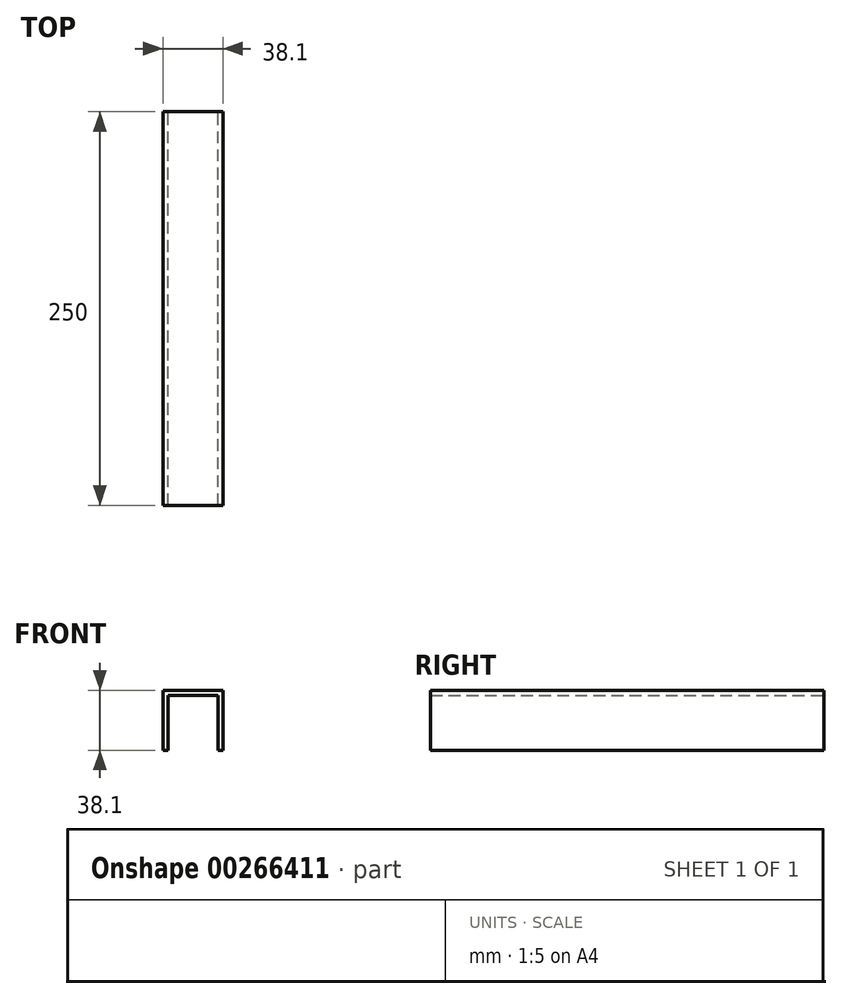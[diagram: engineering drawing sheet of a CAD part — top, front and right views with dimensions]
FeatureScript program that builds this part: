
annotation { "Feature Type Name" : "Feature", "Feature Type Description" : "" }
export const myFeature = defineFeature(function(context is Context, id is Id, definition is map)
    precondition{}
    {
        {
            var Q0;
            Q0=qCreatedBy(makeId("Front.planeOp"),FACE);
            var sketch = newSketch(context, id + "F0", { "sketchPlane" : qUnion([Q0])});
            skLineSegment(sketch, "E0.bottom", {"start": v(19.05, -19.05) * mm, "end": v(-19.05, -19.05) * mm});
            skLineSegment(sketch, "E0.top", {"start": v(19.05, 19.05) * mm, "end": v(-19.05, 19.05) * mm});
            skLineSegment(sketch, "E0.left", {"start": v(19.05, -19.05) * mm, "end": v(19.05, 19.05) * mm});
            skLineSegment(sketch, "E0.right", {"start": v(-19.05, -19.05) * mm, "end": v(-19.05, 19.05) * mm});
            skPoint(sketch, "E0.middle", {"position": v(0, 0) * mm});
            skLineSegment(sketch, "E1", {"start": v(-19.05, -19.05) * mm, "end": v(-15.87, -19.05) * mm, "construction": true});
            skLineSegment(sketch, "E2", {"start": v(19.05, -19.05) * mm, "end": v(15.87, -19.05) * mm, "construction": true});
            skLineSegment(sketch, "E3", {"start": v(-19.05, 19.05) * mm, "end": v(-19.05, 15.87) * mm, "construction": true});
            skLineSegment(sketch, "E4", {"start": v(-15.87, -19.05) * mm, "end": v(-15.87, 15.87) * mm});
            skLineSegment(sketch, "E5", {"start": v(-15.87, 15.87) * mm, "end": v(15.87, 15.87) * mm});
            skLineSegment(sketch, "E6", {"start": v(15.87, 15.87) * mm, "end": v(15.87, -19.05) * mm});
            skSolve(sketch);
        }
        {
            var Q0;
            Q0=makeQuery(id+"F0.imprint","IMPRINT",FACE,{"disambiguationData":[TD([[makeQuery(id+"F0.imprint","IMPRINT",EDGE,{"derivedFrom":sQuery(id+"F0.wireOp",EDGE,"E0.bottom")}),-1.0]])]});
            extrude(context, id + "F1", {"entities" : qUnion([Q0]), "depth" : 125 * mm, "offsetDistance" : 25 * mm, "hasSecondDirection" : true, "secondDirectionOppositeDirection" : true, "secondDirectionDepth" : 125 * mm});
        }
    });
